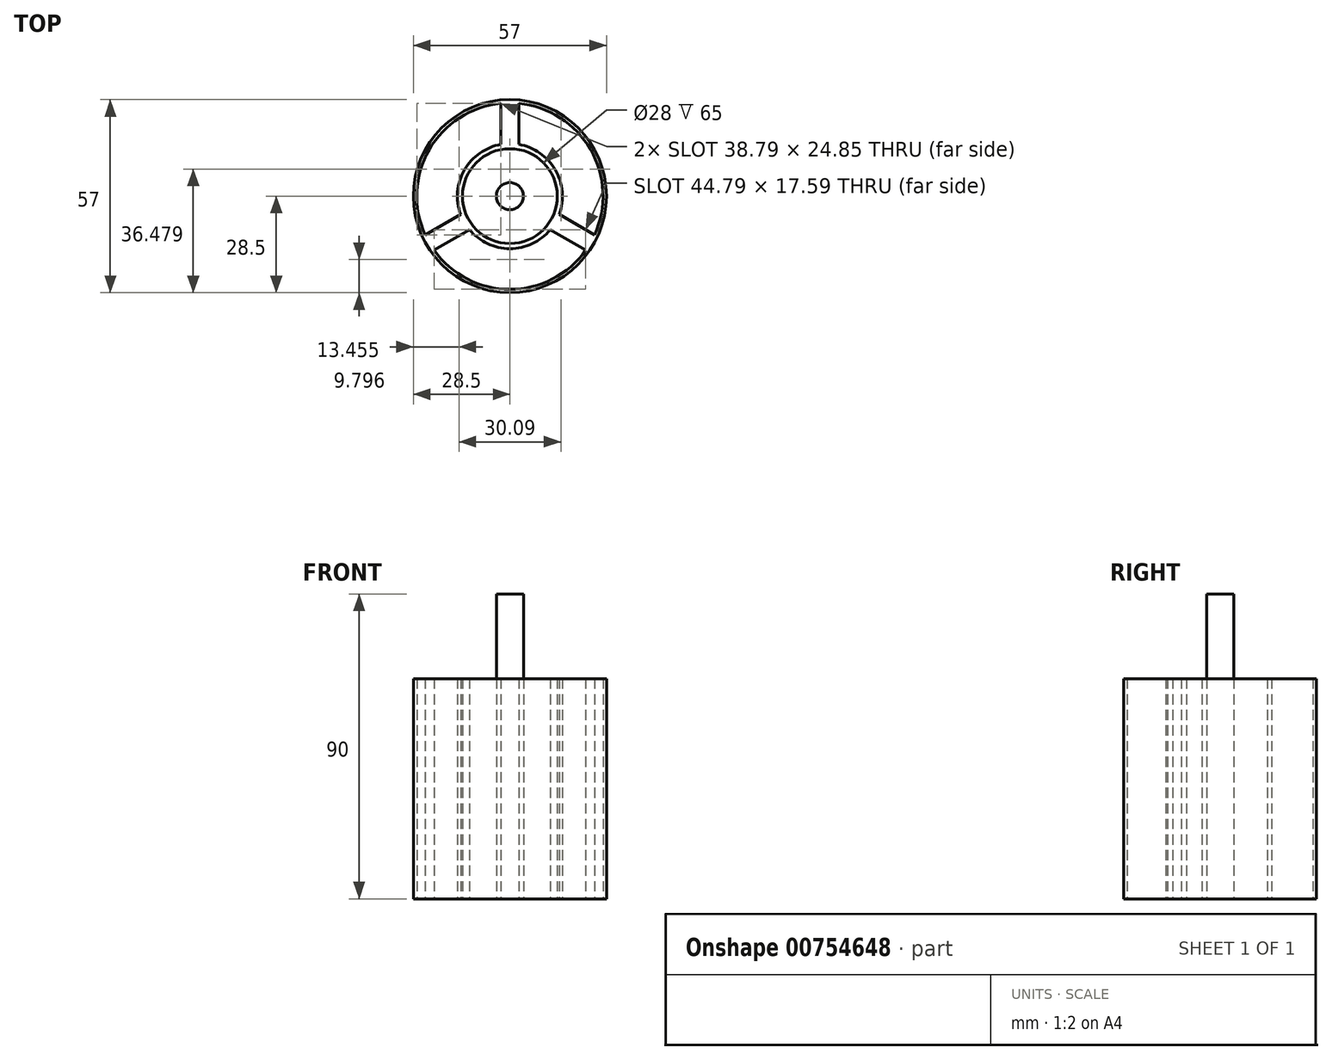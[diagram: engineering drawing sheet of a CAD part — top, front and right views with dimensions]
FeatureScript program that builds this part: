
annotation { "Feature Type Name" : "Feature", "Feature Type Description" : "" }
export const myFeature = defineFeature(function(context is Context, id is Id, definition is map)
    precondition{}
    {
        {
            var Q0;
            Q0=qCreatedBy(makeId("Top.planeOp"),FACE);
            var sketch = newSketch(context, id + "F0", { "sketchPlane" : qUnion([Q0])});
            skCircle(sketch, "E0", {"center": v(0, 0) * mm, "radius": 28.5 * mm});
            skCircle(sketch, "E1", {"center": v(0, 0) * mm, "radius": 27.5 * mm});
            skCircle(sketch, "E2", {"center": v(0, 0) * mm, "radius": 14 * mm});
            skLineSegment(sketch, "E3.left", {"start": v(-2.62, 27.37) * mm, "end": v(-2.62, 13.75) * mm});
            skLineSegment(sketch, "E3.right", {"start": v(2.62, 27.37) * mm, "end": v(2.62, 13.75) * mm});
            skPoint(sketch, "E4.orphan", {"position": v(2.62, 0) * mm});
            skPoint(sketch, "E5.end.orphan", {"position": v(-2.62, 0) * mm});
            skPoint(sketch, "E6.center", {"position": v(0.07, 0.46) * mm});
            skCircle(sketch, "E7", {"center": v(0, 0) * mm, "radius": 15.5 * mm});
            skCircle(sketch, "E8", {"center": v(0, 0) * mm, "radius": 4 * mm});
            skLineSegment(sketch, "E9.1.0", {"start": v(-22.4, -15.96) * mm, "end": v(-10.6, -9.15) * mm});
            skLineSegment(sketch, "E9.1.1", {"start": v(-25.02, -11.42) * mm, "end": v(-13.22, -4.6) * mm});
            skLineSegment(sketch, "E9.2.0", {"start": v(25.02, -11.42) * mm, "end": v(13.22, -4.6) * mm});
            skLineSegment(sketch, "E9.2.1", {"start": v(22.4, -15.96) * mm, "end": v(10.6, -9.15) * mm});
            skSolve(sketch);
        }
        {
            var Q0;
            {var subQ0=sQuery(id+"F0.wireOp",EDGE,"E3.left");var subQ1=sQuery(id+"F0.wireOp",EDGE,"E1");var subQ2=makeQuery(id+"F0.imprint","INTERSECT",VERTEX,{"derivedFrom":[subQ1,subQ0]});Q0=makeQuery(id+"F0.imprint","IMPRINT",FACE,{"disambiguationData":[TD([[makeQuery(id+"F0.imprint","IMPRINT",EDGE,{"disambiguationData":[TD([[subQ2,1.0]])],"derivedFrom":subQ1}),1.0]])]});}
            var Q1;
            {var subQ0=sQuery(id+"F0.wireOp",EDGE,"E9.1.0");var subQ1=sQuery(id+"F0.wireOp",EDGE,"E1");var subQ2=makeQuery(id+"F0.imprint","INTERSECT",VERTEX,{"derivedFrom":[subQ1,subQ0]});Q1=makeQuery(id+"F0.imprint","IMPRINT",FACE,{"disambiguationData":[TD([[makeQuery(id+"F0.imprint","IMPRINT",EDGE,{"disambiguationData":[TD([[subQ2,1.0]])],"derivedFrom":subQ1}),1.0]])]});}
            var Q2;
            {var subQ0=sQuery(id+"F0.wireOp",EDGE,"E9.2.0");var subQ1=sQuery(id+"F0.wireOp",EDGE,"E1");var subQ2=makeQuery(id+"F0.imprint","INTERSECT",VERTEX,{"derivedFrom":[subQ1,subQ0]});Q2=makeQuery(id+"F0.imprint","IMPRINT",FACE,{"disambiguationData":[TD([[makeQuery(id+"F0.imprint","IMPRINT",EDGE,{"disambiguationData":[TD([[subQ2,1.0]])],"derivedFrom":subQ1}),1.0]])]});}
            var Q3;
            Q3=makeQuery(id+"F0.imprint","IMPRINT",FACE,{"disambiguationData":[TD([[makeQuery(id+"F0.imprint","IMPRINT",EDGE,{"derivedFrom":sQuery(id+"F0.wireOp",EDGE,"E0")}),1.0]])]});
            var Q4;
            {var subQ0=sQuery(id+"F0.wireOp",EDGE,"E3.left");var subQ1=sQuery(id+"F0.wireOp",EDGE,"E2");var subQ2=makeQuery(id+"F0.imprint","INTERSECT",VERTEX,{"derivedFrom":[subQ1,subQ0]});Q4=makeQuery(id+"F0.imprint","IMPRINT",FACE,{"disambiguationData":[TD([[makeQuery(id+"F0.imprint","IMPRINT",EDGE,{"disambiguationData":[TD([[subQ2,-1.0]])],"derivedFrom":subQ1}),-1.0]])]});}
            var Q5;
            {var subQ0=sQuery(id+"F0.wireOp",EDGE,"E3.left");var subQ1=sQuery(id+"F0.wireOp",EDGE,"E2");var subQ2=makeQuery(id+"F0.imprint","INTERSECT",VERTEX,{"derivedFrom":[subQ1,subQ0]});Q5=makeQuery(id+"F0.imprint","IMPRINT",FACE,{"disambiguationData":[TD([[makeQuery(id+"F0.imprint","IMPRINT",EDGE,{"disambiguationData":[TD([[subQ2,1.0]])],"derivedFrom":subQ1}),-1.0]])]});}
            var Q6;
            {var subQ0=sQuery(id+"F0.wireOp",EDGE,"E3.right");var subQ1=sQuery(id+"F0.wireOp",EDGE,"E2");var subQ2=makeQuery(id+"F0.imprint","INTERSECT",VERTEX,{"derivedFrom":[subQ1,subQ0]});Q6=makeQuery(id+"F0.imprint","IMPRINT",FACE,{"disambiguationData":[TD([[makeQuery(id+"F0.imprint","IMPRINT",EDGE,{"disambiguationData":[TD([[subQ2,1.0]])],"derivedFrom":subQ1}),-1.0]])]});}
            var Q7;
            {var subQ0=sQuery(id+"F0.wireOp",EDGE,"E9.1.0");var subQ1=sQuery(id+"F0.wireOp",EDGE,"E2");var subQ2=makeQuery(id+"F0.imprint","INTERSECT",VERTEX,{"derivedFrom":[subQ1,subQ0]});Q7=makeQuery(id+"F0.imprint","IMPRINT",FACE,{"disambiguationData":[TD([[makeQuery(id+"F0.imprint","IMPRINT",EDGE,{"disambiguationData":[TD([[subQ2,1.0]])],"derivedFrom":subQ1}),-1.0]])]});}
            var Q8;
            {var subQ0=sQuery(id+"F0.wireOp",EDGE,"E9.1.0");var subQ1=sQuery(id+"F0.wireOp",EDGE,"E2");var subQ2=makeQuery(id+"F0.imprint","INTERSECT",VERTEX,{"derivedFrom":[subQ1,subQ0]});Q8=makeQuery(id+"F0.imprint","IMPRINT",FACE,{"disambiguationData":[TD([[makeQuery(id+"F0.imprint","IMPRINT",EDGE,{"disambiguationData":[TD([[subQ2,-1.0]])],"derivedFrom":subQ1}),-1.0]])]});}
            var Q9;
            {var subQ0=sQuery(id+"F0.wireOp",EDGE,"E9.2.0");var subQ1=sQuery(id+"F0.wireOp",EDGE,"E2");var subQ2=makeQuery(id+"F0.imprint","INTERSECT",VERTEX,{"derivedFrom":[subQ1,subQ0]});Q9=makeQuery(id+"F0.imprint","IMPRINT",FACE,{"disambiguationData":[TD([[makeQuery(id+"F0.imprint","IMPRINT",EDGE,{"disambiguationData":[TD([[subQ2,1.0]])],"derivedFrom":subQ1}),-1.0]])]});}
            extrude(context, id + "F1", {"entities" : qUnion([Q0, Q1, Q2, Q3, Q4, Q5, Q6, Q7, Q8, Q9]), "depth" : 65 * mm, "offsetDistance" : 25 * mm});
        }
        {
            var Q0;
            Q0=makeQuery(id+"F0.imprint","IMPRINT",FACE,{"disambiguationData":[TD([[makeQuery(id+"F0.imprint","IMPRINT",EDGE,{"derivedFrom":sQuery(id+"F0.wireOp",EDGE,"E8")}),1.0]])]});
            extrude(context, id + "F2", {"entities" : qUnion([Q0]), "depth" : 90 * mm, "offsetDistance" : 25 * mm});
        }
    });
